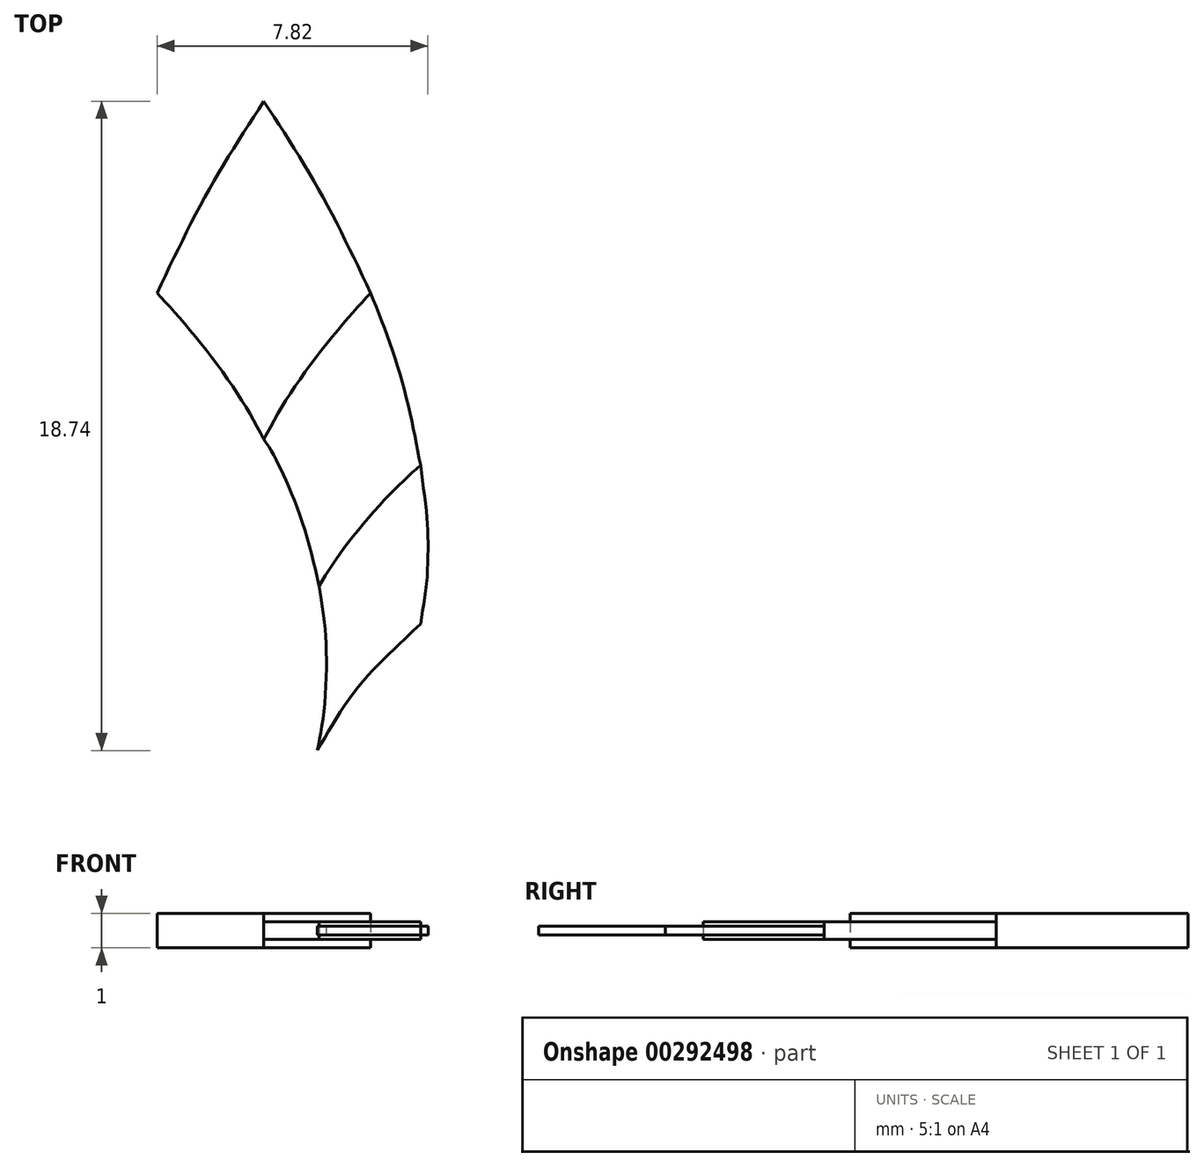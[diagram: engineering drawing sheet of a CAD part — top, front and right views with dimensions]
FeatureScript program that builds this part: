
annotation { "Feature Type Name" : "Feature", "Feature Type Description" : "" }
export const myFeature = defineFeature(function(context is Context, id is Id, definition is map)
    precondition{}
    {
        {
            var Q0;
            Q0=qCreatedBy(makeId("Top.planeOp"),FACE);
            var sketch = newSketch(context, id + "F0", { "sketchPlane" : qUnion([Q0])});
            skFitSpline(sketch, "E0", {"points": [v(33.46, -17.35) * mm, v(35.08, -19.95) * mm, v(36.55, -22.89) * mm], "startDerivative": vector(3.38, -5.18) * mm, "endDerivative": vector(2.8, -5.88) * mm});
            skLineSegment(sketch, "E1", {"start": v(33.46, -17.35) * mm, "end": v(33.46, -42.46) * mm});
            skFitSpline(sketch, "E2", {"points": [v(36.55, -22.89) * mm, v(35.9, -23.6) * mm, v(34.93, -24.8) * mm, v(34.03, -26.1) * mm, v(33.46, -27.1) * mm], "startDerivative": vector(-2.86, -3.05) * mm, "endDerivative": vector(-2.2, -4.12) * mm});
            skFitSpline(sketch, "E3.MirrorCS", {"points": [v(30.38, -22.89) * mm, v(31.02, -23.6) * mm, v(32, -24.8) * mm, v(32.9, -26.1) * mm, v(33.46, -27.1) * mm], "startDerivative": vector(2.86, -3.05) * mm, "endDerivative": vector(2.2, -4.12) * mm});
            skFitSpline(sketch, "E4.MirrorCS", {"points": [v(33.46, -17.35) * mm, v(31.85, -19.95) * mm, v(30.38, -22.89) * mm], "startDerivative": vector(-3.38, -5.18) * mm, "endDerivative": vector(-2.8, -5.88) * mm});
            skLineSegment(sketch, "E5", {"start": v(42.53, -40.25) * mm, "end": v(30.43, -40.25) * mm});
            skSolve(sketch);
        }
        {
            var Q0;
            Q0=qCreatedBy(makeId("Top.planeOp"),FACE);
            var sketch = newSketch(context, id + "F1", { "sketchPlane" : qUnion([Q0])});
            skFitSpline(sketch, "E6", {"points": [v(35.05, -31.34) * mm, v(35.81, -30.2) * mm, v(37.1, -28.7) * mm, v(37.99, -27.85) * mm], "startDerivative": vector(2.1, 3.42) * mm, "endDerivative": vector(2.77, 2.5) * mm});
            skFitSpline(sketch, "E7", {"points": [v(37.99, -27.85) * mm, v(37.67, -26.27) * mm, v(37.15, -24.45) * mm, v(36.55, -22.89) * mm], "startDerivative": vector(-0.88, 4.78) * mm, "endDerivative": vector(-1.79, 4.54) * mm});
            skFitSpline(sketch, "E8", {"points": [v(35.05, -31.34) * mm, v(34.64, -29.69) * mm, v(34.11, -28.31) * mm, v(33.75, -27.57) * mm, v(33.46, -27.1) * mm], "startDerivative": vector(-1.17, 5.35) * mm, "endDerivative": vector(-1.6, 2.52) * mm});
            skFitSpline(sketch, "E9", {"points": [v(36.55, -22.89) * mm, v(35.9, -23.6) * mm, v(34.93, -24.8) * mm, v(34.03, -26.1) * mm, v(33.46, -27.1) * mm], "startDerivative": vector(-2.86, -3.05) * mm, "endDerivative": vector(-2.2, -4.12) * mm});
            skSolve(sketch);
        }
        {
            var Q0;
            Q0=qCreatedBy(makeId("Top.planeOp"),FACE);
            var sketch = newSketch(context, id + "F2", { "sketchPlane" : qUnion([Q0])});
            skFitSpline(sketch, "E10", {"points": [v(35, -36.09) * mm, v(35.18, -35.14) * mm, v(35.27, -33.44) * mm, v(35.18, -32.17) * mm, v(35.05, -31.34) * mm], "startDerivative": vector(0.78, 3.8) * mm, "endDerivative": vector(-0.56, 3.64) * mm});
            skFitSpline(sketch, "E11", {"points": [v(35, -36.09) * mm, v(35.53, -35.2) * mm, v(36.18, -34.27) * mm, v(36.86, -33.52) * mm, v(37.58, -32.82) * mm, v(37.99, -32.43) * mm], "startDerivative": vector(2.4, 4.2) * mm, "endDerivative": vector(2.63, 2.27) * mm});
            skFitSpline(sketch, "E12", {"points": [v(37.99, -32.43) * mm, v(38.15, -31.37) * mm, v(38.2, -30.22) * mm, v(38.16, -29.24) * mm, v(37.99, -27.85) * mm], "startDerivative": vector(0.6, 4.25) * mm, "endDerivative": vector(-0.59, 5.13) * mm});
            skFitSpline(sketch, "E13", {"points": [v(35.05, -31.34) * mm, v(35.81, -30.2) * mm, v(37.1, -28.7) * mm, v(37.99, -27.85) * mm], "startDerivative": vector(2.1, 3.42) * mm, "endDerivative": vector(2.77, 2.5) * mm});
            skSolve(sketch);
        }
        {
            var Q0;
            {var subQ0=sQuery(id+"F0.wireOp",EDGE,"E0");Q0=makeQuery(id+"F0.imprint","IMPRINT",FACE,{"disambiguationData":[TD([[makeQuery(id+"F0.imprint","IMPRINT",EDGE,{"derivedFrom":subQ0}),-1.0]])]});}
            var Q1;
            {var subQ2=sQuery(id+"F0.wireOp",EDGE,"E3.MirrorCS");Q1=makeQuery(id+"F0.imprint","IMPRINT",FACE,{"disambiguationData":[TD([[makeQuery(id+"F0.imprint","IMPRINT",EDGE,{"derivedFrom":subQ2}),1.0]])]});}
            extrude(context, id + "F3", {"entities" : qUnion([Q0, Q1]), "endBound" : BoundingType.SYMMETRIC, "depth" : 1 * mm});
        }
        {
            var Q0;
            Q0=makeQuery(id+"F1.imprint","IMPRINT",FACE,{"disambiguationData":[TD([[makeQuery(id+"F1.imprint","IMPRINT",EDGE,{"derivedFrom":sQuery(id+"F1.wireOp",EDGE,"E6")}),1.0]])]});
            extrude(context, id + "F4", {"entities" : qUnion([Q0]), "operationType" : NewBodyOperationType.ADD, "endBound" : BoundingType.SYMMETRIC, "depth" : 0.5 * mm});
        }
        {
            var Q0;
            Q0=makeQuery(id+"F2.imprint","IMPRINT",FACE,{"disambiguationData":[TD([[makeQuery(id+"F2.imprint","IMPRINT",EDGE,{"derivedFrom":sQuery(id+"F2.wireOp",EDGE,"E10")}),-1.0]])]});
            extrude(context, id + "F5", {"entities" : qUnion([Q0]), "operationType" : NewBodyOperationType.ADD, "endBound" : BoundingType.SYMMETRIC, "depth" : 0.25 * mm});
        }
        {
            var Q0;
            Q0=qCreatedBy(makeId("Right.planeOp"),FACE);
            cPlane(context, id + "F6", {"entities" : qUnion([Q0]), "cplaneType" : CPlaneType.OFFSET, "offset" : 33.46 * mm, "width" : 150 * mm, "height" : 150 * mm});
        }
    });
